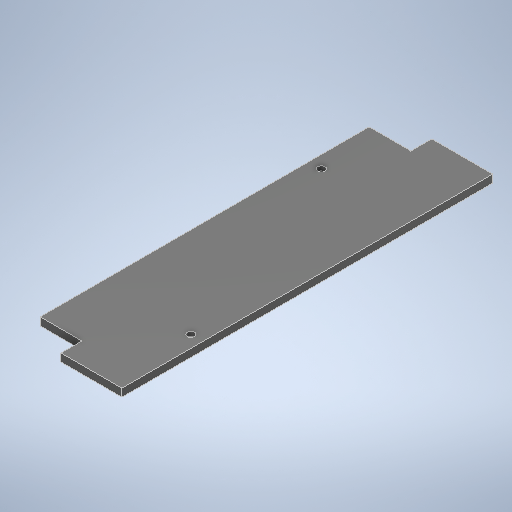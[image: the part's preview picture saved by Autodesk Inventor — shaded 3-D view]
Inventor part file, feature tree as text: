
AUTODESK INVENTOR PART (.ipt)
format: ipt  version: 2025 (Build 290162000, 162)  size: 245,760 bytes
history: native  units: mm
features: sketch x3, extrude x2, hole x1
ambient origin geometry x8: Origin, YZ Plane, XZ Plane, XY Plane, X Axis, Y Axis, Z Axis, Center Point
bodies: Solid1 (feature_tree)
feature tree (6):
  extrude  "Extrusion1"  Depth=125.0mm
  extrude  "Extrusion2"  Depth=25.4mm
  hole  "Hole1"  [1 undecoded]
  sketch  "Sketch1"  dims[d0=451.4mm d1=125.0mm]
  sketch  "Sketch2"  dims[d2=9.525mm d3=0.0mm d4=25.4mm]
  sketch  "Sketch3"  dims[d5=25.4mm d6=50.8mm d7=50.8mm d8=0.0mm d9=0.0mm d10=254.0mm d11=95.2mm d12=127.0mm d13=15.0mm d14=14.8mm d15=9.0mm d16=16.0mm d17=17.3mm d18=2.0mm d19=90.0deg d20=8.0mm d21=20.594885mm]
note: 1 required parameter value undecoded (feature->parameter linkage not recoverable at this tier; creation-order binding heuristic only, values carry confidence <= 0.55)
